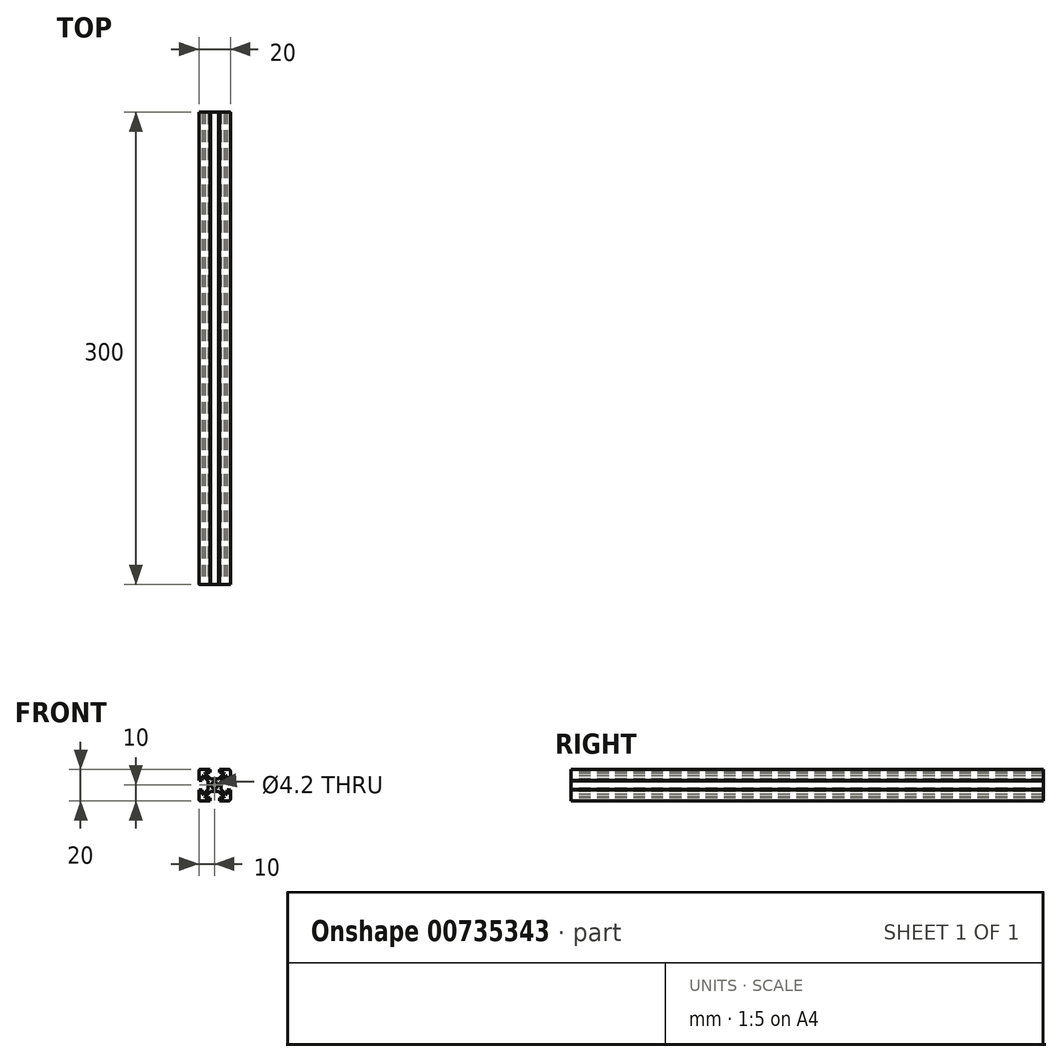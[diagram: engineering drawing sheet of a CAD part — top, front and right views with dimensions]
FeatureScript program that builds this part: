
annotation { "Feature Type Name" : "Feature", "Feature Type Description" : "" }
export const myFeature = defineFeature(function(context is Context, id is Id, definition is map)
    precondition{}
    {
        {
            var Q0;
            Q0=qCreatedBy(makeId("Front.planeOp"),FACE);
            var sketch = newSketch(context, id + "F0", { "sketchPlane" : qUnion([Q0])});
            skLineSegment(sketch, "E0", {"start": v(0, 4) * mm, "end": v(2.59, 4) * mm});
            skLineSegment(sketch, "E1", {"start": v(6, 8) * mm, "end": v(3, 8) * mm});
            skLineSegment(sketch, "E2", {"start": v(3, 8) * mm, "end": v(3, 10) * mm});
            skLineSegment(sketch, "E3", {"start": v(3, 10) * mm, "end": v(10, 10) * mm});
            skLineSegment(sketch, "E4", {"start": v(10, 10) * mm, "end": v(10, 3) * mm});
            skLineSegment(sketch, "E5", {"start": v(10, 3) * mm, "end": v(8, 3) * mm});
            skLineSegment(sketch, "E6", {"start": v(8, 3) * mm, "end": v(8, 6) * mm});
            skLineSegment(sketch, "E7", {"start": v(4, 2.59) * mm, "end": v(4, 0) * mm});
            skLineSegment(sketch, "E8", {"start": v(6, 8) * mm, "end": v(6, 7.41) * mm});
            skLineSegment(sketch, "E9", {"start": v(6, 7.41) * mm, "end": v(2.59, 4) * mm});
            skLineSegment(sketch, "E10", {"start": v(8, 6) * mm, "end": v(7.41, 6) * mm});
            skLineSegment(sketch, "E11", {"start": v(7.41, 6) * mm, "end": v(4, 2.59) * mm});
            skLineSegment(sketch, "E12.MirrorCS", {"start": v(-6, 8) * mm, "end": v(-6, 7.41) * mm});
            skLineSegment(sketch, "E13.MirrorCS", {"start": v(-8, 6) * mm, "end": v(-7.41, 6) * mm});
            skLineSegment(sketch, "E14.MirrorCS", {"start": v(-10, 3) * mm, "end": v(-8, 3) * mm});
            skLineSegment(sketch, "E15.MirrorCS", {"start": v(-8, 3) * mm, "end": v(-8, 6) * mm});
            skLineSegment(sketch, "E16.MirrorCS", {"start": v(-7.41, 6) * mm, "end": v(-4, 2.59) * mm});
            skLineSegment(sketch, "E17.MirrorCS", {"start": v(-6, 7.41) * mm, "end": v(-2.59, 4) * mm});
            skLineSegment(sketch, "E18.MirrorCS", {"start": v(-6, 8) * mm, "end": v(-3, 8) * mm});
            skLineSegment(sketch, "E19.MirrorCS", {"start": v(-10, 10) * mm, "end": v(-10, 3) * mm});
            skLineSegment(sketch, "E20.MirrorCS", {"start": v(-3, 8) * mm, "end": v(-3, 10) * mm});
            skLineSegment(sketch, "E21.MirrorCS", {"start": v(0, 4) * mm, "end": v(-2.59, 4) * mm});
            skLineSegment(sketch, "E22.MirrorCS", {"start": v(-4, 2.59) * mm, "end": v(-4, 0) * mm});
            skLineSegment(sketch, "E23.MirrorCS", {"start": v(-3, 10) * mm, "end": v(-10, 10) * mm});
            skLineSegment(sketch, "E24.MirrorCS", {"start": v(10, -3) * mm, "end": v(8, -3) * mm});
            skLineSegment(sketch, "E25.MirrorCS", {"start": v(-10, -3) * mm, "end": v(-8, -3) * mm});
            skLineSegment(sketch, "E26.MirrorCS", {"start": v(3, -8) * mm, "end": v(3, -10) * mm});
            skLineSegment(sketch, "E27.MirrorCS", {"start": v(-3, -8) * mm, "end": v(-3, -10) * mm});
            skLineSegment(sketch, "E28.MirrorCS", {"start": v(6, -8) * mm, "end": v(6, -7.41) * mm});
            skLineSegment(sketch, "E29.MirrorCS", {"start": v(-6, -8) * mm, "end": v(-6, -7.41) * mm});
            skLineSegment(sketch, "E30.MirrorCS", {"start": v(-8, -6) * mm, "end": v(-7.41, -6) * mm});
            skLineSegment(sketch, "E31.MirrorCS", {"start": v(8, -6) * mm, "end": v(7.41, -6) * mm});
            skLineSegment(sketch, "E32.MirrorCS", {"start": v(3, -10) * mm, "end": v(10, -10) * mm});
            skLineSegment(sketch, "E33.MirrorCS", {"start": v(-10, -10) * mm, "end": v(-10, -3) * mm});
            skLineSegment(sketch, "E34.MirrorCS", {"start": v(-4, -2.59) * mm, "end": v(-4, 0) * mm});
            skLineSegment(sketch, "E35.MirrorCS", {"start": v(-3, -10) * mm, "end": v(-10, -10) * mm});
            skLineSegment(sketch, "E36.MirrorCS", {"start": v(7.41, -6) * mm, "end": v(4, -2.59) * mm});
            skLineSegment(sketch, "E37.MirrorCS", {"start": v(0, -4) * mm, "end": v(-2.59, -4) * mm});
            skLineSegment(sketch, "E38.MirrorCS", {"start": v(6, -8) * mm, "end": v(3, -8) * mm});
            skLineSegment(sketch, "E39.MirrorCS", {"start": v(4, -2.59) * mm, "end": v(4, 0) * mm});
            skLineSegment(sketch, "E40.MirrorCS", {"start": v(10, -10) * mm, "end": v(10, -3) * mm});
            skLineSegment(sketch, "E41.MirrorCS", {"start": v(-7.41, -6) * mm, "end": v(-4, -2.59) * mm});
            skLineSegment(sketch, "E42.MirrorCS", {"start": v(6, -7.41) * mm, "end": v(2.59, -4) * mm});
            skLineSegment(sketch, "E43.MirrorCS", {"start": v(8, -3) * mm, "end": v(8, -6) * mm});
            skLineSegment(sketch, "E44.MirrorCS", {"start": v(-6, -7.41) * mm, "end": v(-2.59, -4) * mm});
            skLineSegment(sketch, "E45.MirrorCS", {"start": v(-6, -8) * mm, "end": v(-3, -8) * mm});
            skLineSegment(sketch, "E46.MirrorCS", {"start": v(-8, -3) * mm, "end": v(-8, -6) * mm});
            skLineSegment(sketch, "E47.MirrorCS", {"start": v(0, -4) * mm, "end": v(2.59, -4) * mm});
            skCircle(sketch, "E48", {"center": v(0, 0) * mm, "radius": 2.1 * mm});
            skSolve(sketch);
        }
        {
            var Q0;
            Q0=makeQuery(id+"F0.imprint","IMPRINT",FACE,{"disambiguationData":[TD([[makeQuery(id+"F0.imprint","IMPRINT",EDGE,{"derivedFrom":sQuery(id+"F0.wireOp",EDGE,"E0")}),-1.0]])]});
            extrude(context, id + "F1", {"entities" : qUnion([Q0]), "oppositeDirection" : true, "depth" : 300 * mm, "offsetDistance" : 25 * mm});
        }
        {
            var Q0;
            Q0=makeQuery(id+"F1.opExtrude","SWEPT_EDGE",EDGE,{"disambiguationData":[OSD([sQuery(id+"F0.wireOp",EDGE,"E19.MirrorCS"),sQuery(id+"F0.wireOp",EDGE,"E23.MirrorCS")])]});
            var Q1;
            Q1=makeQuery(id+"F1.opExtrude","SWEPT_EDGE",EDGE,{"disambiguationData":[OSD([sQuery(id+"F0.wireOp",EDGE,"E3"),sQuery(id+"F0.wireOp",EDGE,"E4")])]});
            var Q2;
            Q2=makeQuery(id+"F1.opExtrude","SWEPT_EDGE",EDGE,{"disambiguationData":[OSD([sQuery(id+"F0.wireOp",EDGE,"E32.MirrorCS"),sQuery(id+"F0.wireOp",EDGE,"E40.MirrorCS")])]});
            var Q3;
            Q3=makeQuery(id+"F1.opExtrude","SWEPT_EDGE",EDGE,{"disambiguationData":[OSD([sQuery(id+"F0.wireOp",EDGE,"E33.MirrorCS"),sQuery(id+"F0.wireOp",EDGE,"E35.MirrorCS")])]});
            fillet(context, id + "F2", {"entities" : qUnion([Q0, Q1, Q2, Q3]), "radius" : 1 * mm, "tangentPropagation" : true, "allowEdgeOverflow" : false});
        }
    });
